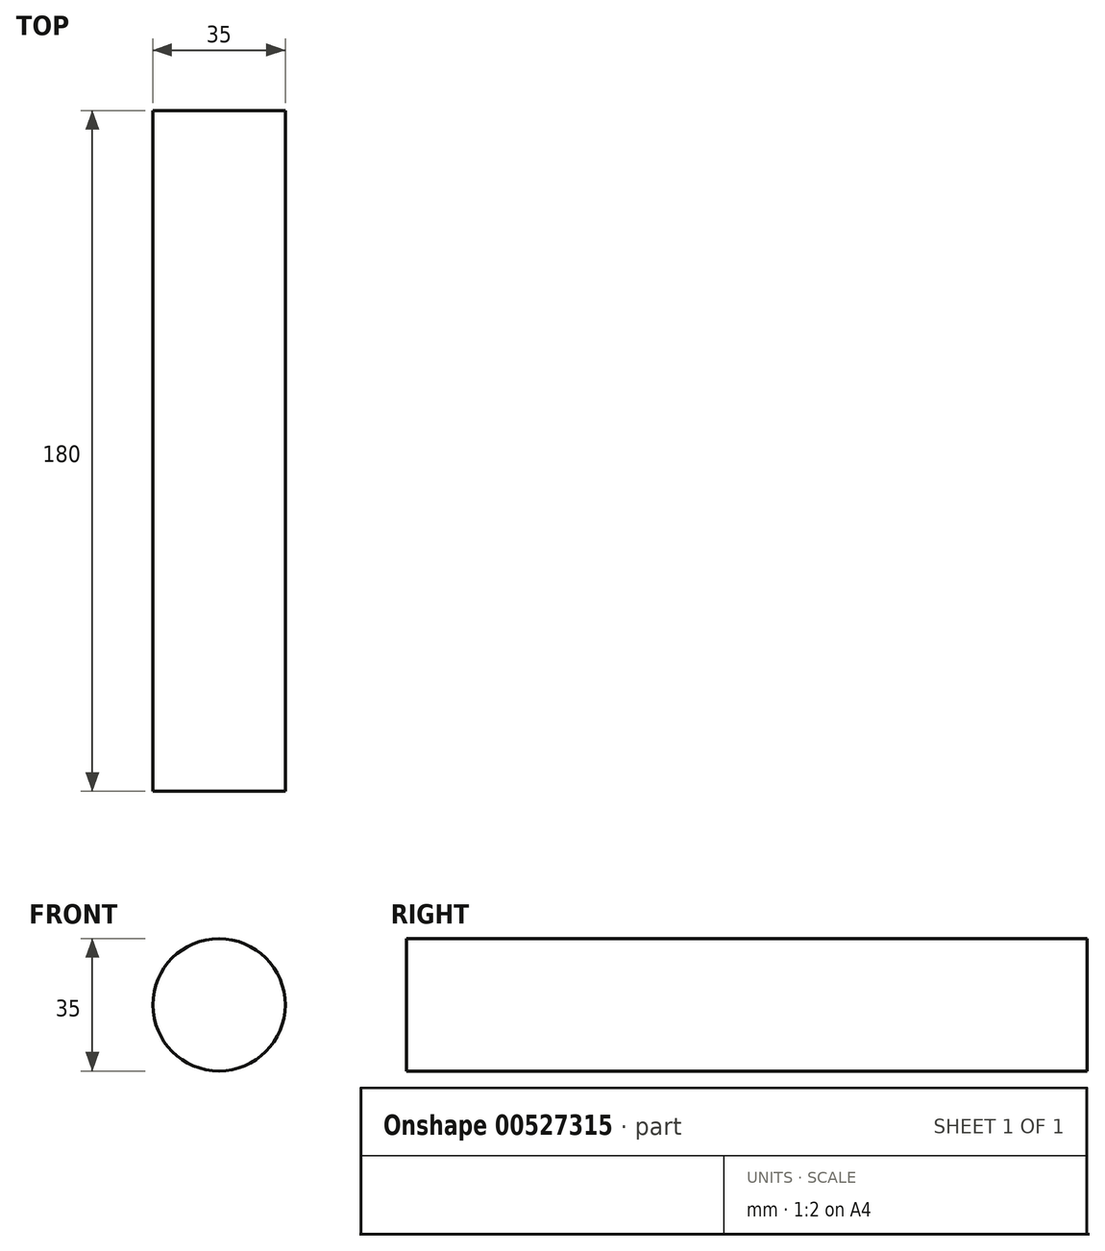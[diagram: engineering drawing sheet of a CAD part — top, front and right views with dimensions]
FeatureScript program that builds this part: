
annotation { "Feature Type Name" : "Feature", "Feature Type Description" : "" }
export const myFeature = defineFeature(function(context is Context, id is Id, definition is map)
    precondition{}
    {
        {
            var Q0;
            Q0=qCreatedBy(makeId("Front.planeOp"),FACE);
            var sketch = newSketch(context, id + "F0", { "sketchPlane" : qUnion([Q0])});
            skCircle(sketch, "E0", {"center": v(0, 0) * mm, "radius": 17.5 * mm});
            skSolve(sketch);
        }
        {
            var Q0;
            Q0 = qSketchRegion(id + "F0", true);
            extrude(context, id + "F1", {"entities" : qUnion([Q0]), "depth" : 180 * mm, "offsetDistance" : 25 * mm});
        }
    });
